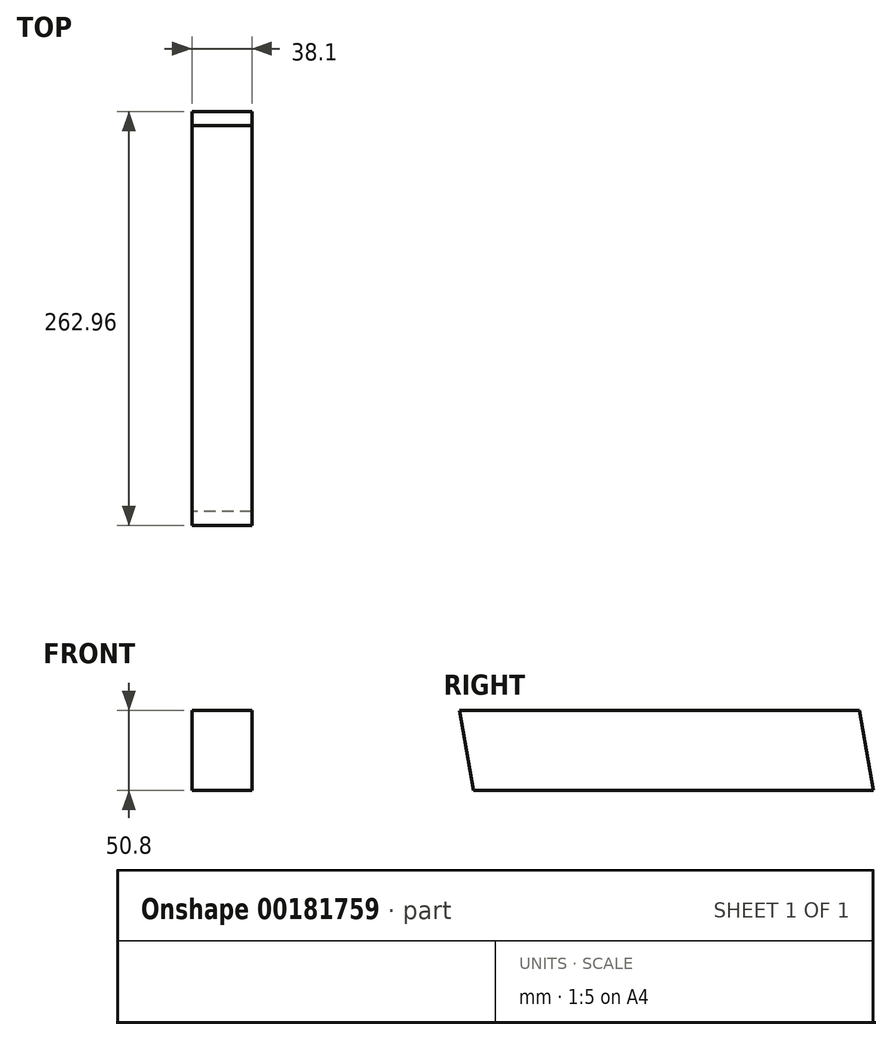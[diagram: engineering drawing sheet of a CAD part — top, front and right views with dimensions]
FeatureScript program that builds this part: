
annotation { "Feature Type Name" : "Feature", "Feature Type Description" : "" }
export const myFeature = defineFeature(function(context is Context, id is Id, definition is map)
    precondition{}
    {
        {
            var Q0;
            Q0=qCreatedBy(makeId("Right.planeOp"),FACE);
            var sketch = newSketch(context, id + "F0", { "sketchPlane" : qUnion([Q0])});
            skLineSegment(sketch, "E0.bottom", {"start": v(-87.7, 0) * mm, "end": v(166.3, 0) * mm});
            skLineSegment(sketch, "E0.top", {"start": v(-96.67, 50.8) * mm, "end": v(157.33, 50.8) * mm});
            skLineSegment(sketch, "E1", {"start": v(166.3, 0) * mm, "end": v(157.33, 50.8) * mm});
            skLineSegment(sketch, "E2", {"start": v(-96.67, 50.8) * mm, "end": v(-87.7, 0) * mm});
            skPoint(sketch, "E3.orphan", {"position": v(-105.86, 0) * mm});
            skSolve(sketch);
        }
        {
            var Q0;
            Q0 = qSketchRegion(id + "F0", true);
            extrude(context, id + "F1", {"entities" : qUnion([Q0]), "depth" : 38.1 * mm});
        }
    });
